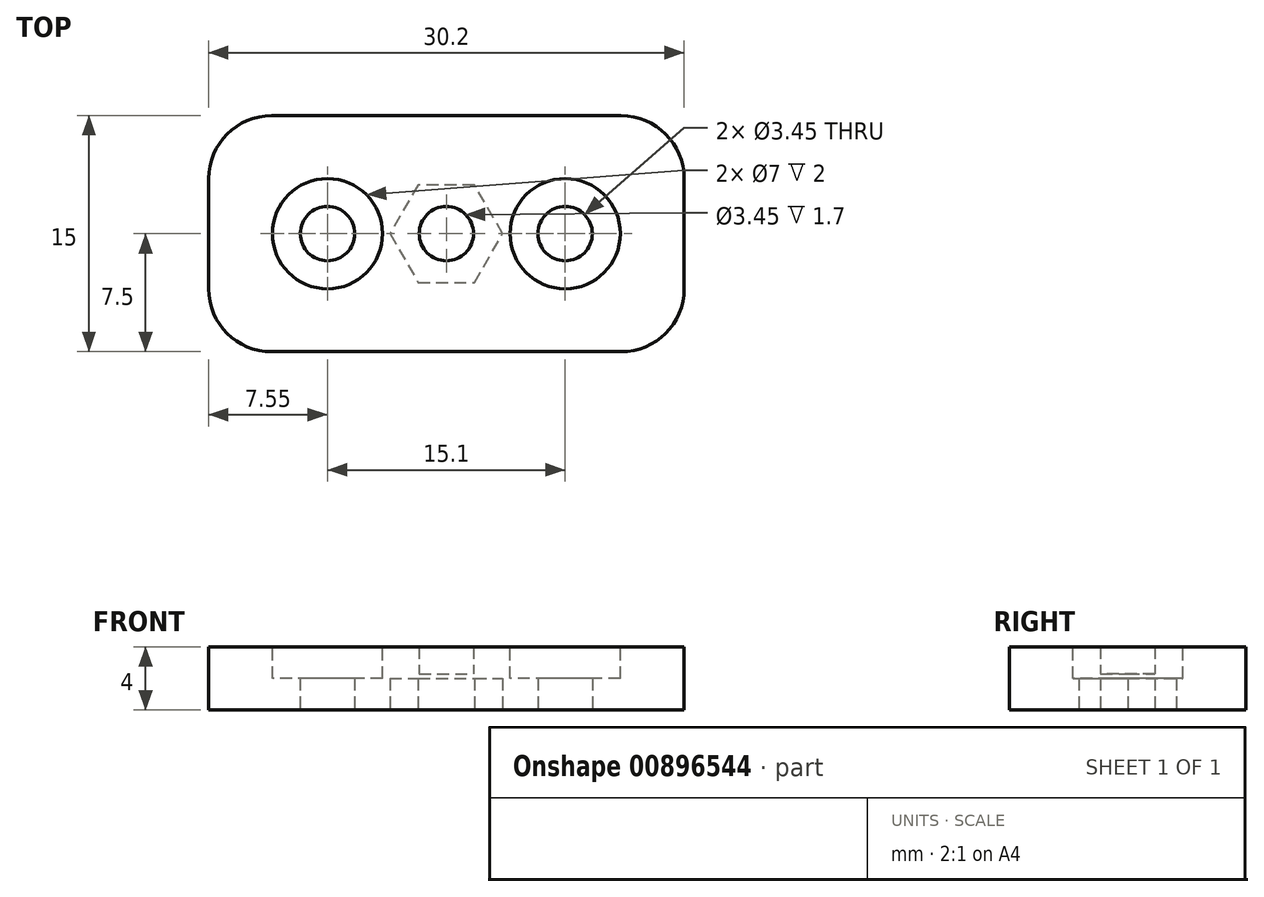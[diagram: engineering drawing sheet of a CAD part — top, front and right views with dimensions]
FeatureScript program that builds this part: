
annotation { "Feature Type Name" : "Feature", "Feature Type Description" : "" }
export const myFeature = defineFeature(function(context is Context, id is Id, definition is map)
    precondition{}
    {
        {
            var Q0;
            Q0=qCreatedBy(makeId("Top.planeOp"),FACE);
            var sketch = newSketch(context, id + "F0", { "sketchPlane" : qUnion([Q0])});
            skLineSegment(sketch, "E0.bottom", {"start": v(0, 0) * mm, "end": v(30.2, 0) * mm});
            skLineSegment(sketch, "E0.top", {"start": v(0, 15) * mm, "end": v(30.2, 15) * mm});
            skLineSegment(sketch, "E0.left", {"start": v(0, 0) * mm, "end": v(0, 15) * mm});
            skLineSegment(sketch, "E0.right", {"start": v(30.2, 0) * mm, "end": v(30.2, 15) * mm});
            skLineSegment(sketch, "E1", {"start": v(15.1, 0) * mm, "end": v(15.1, 15) * mm, "construction": true});
            skCircle(sketch, "E2", {"center": v(7.55, 7.5) * mm, "radius": 1.73 * mm});
            skCircle(sketch, "E3", {"center": v(22.65, 7.5) * mm, "radius": 1.73 * mm});
            skLineSegment(sketch, "E4", {"start": v(7.55, 7.5) * mm, "end": v(15.1, 7.5) * mm, "construction": true});
            skLineSegment(sketch, "E5", {"start": v(15.1, 7.5) * mm, "end": v(22.65, 7.5) * mm, "construction": true});
            skCircle(sketch, "E6", {"center": v(15.1, 7.5) * mm, "radius": 1.73 * mm});
            skSolve(sketch);
        }
        {
            var Q0;
            Q0 = qSketchRegion(id + "F0", true);
            extrude(context, id + "F1", {"entities" : qUnion([Q0]), "depth" : 4 * mm, "offsetDistance" : 25 * mm});
        }
        {
            var Q0;
            Q0=makeQuery(id+"F1.opExtrude","CAP_FACE",FACE,{"disambiguationData":[OSD([sQuery(id+"F0.wireOp",EDGE,"E0.bottom"),sQuery(id+"F0.wireOp",EDGE,"E0.top"),sQuery(id+"F0.wireOp",EDGE,"E0.left"),sQuery(id+"F0.wireOp",EDGE,"E0.right"),sQuery(id+"F0.wireOp",EDGE,"E2"),sQuery(id+"F0.wireOp",EDGE,"E3"),sQuery(id+"F0.wireOp",EDGE,"E6")])],"isStart":false});
            var sketch = newSketch(context, id + "F2", { "sketchPlane" : qUnion([Q0])});
            skCircle(sketch, "E7", {"center": v(7.55, 7.5) * mm, "radius": 3.5 * mm});
            skCircle(sketch, "E8", {"center": v(22.65, 7.5) * mm, "radius": 3.5 * mm});
            skSolve(sketch);
        }
        {
            var Q0;
            Q0 = qSketchRegion(id + "F2", true);
            extrude(context, id + "F3", {"entities" : qUnion([Q0]), "operationType" : NewBodyOperationType.REMOVE, "oppositeDirection" : true, "depth" : 2 * mm, "offsetDistance" : 25 * mm});
        }
        {
            var Q0;
            Q0=makeQuery(id+"F1.opExtrude","CAP_FACE",FACE,{"disambiguationData":[OSD([sQuery(id+"F0.wireOp",EDGE,"E0.bottom"),sQuery(id+"F0.wireOp",EDGE,"E0.top"),sQuery(id+"F0.wireOp",EDGE,"E0.left"),sQuery(id+"F0.wireOp",EDGE,"E0.right"),sQuery(id+"F0.wireOp",EDGE,"E2"),sQuery(id+"F0.wireOp",EDGE,"E3"),sQuery(id+"F0.wireOp",EDGE,"E6")])],"isStart":true});
            var sketch = newSketch(context, id + "F4", { "sketchPlane" : qUnion([Q0])});
            skCircle(sketch, "E9.cCircle", {"center": v(15.1, -7.5) * mm, "radius": 3.1 * mm, "construction": true});
            skLineSegment(sketch, "E9.0", {"start": v(16.89, -4.4) * mm, "end": v(18.68, -7.5) * mm});
            skLineSegment(sketch, "E9.1", {"start": v(18.68, -7.5) * mm, "end": v(16.89, -10.6) * mm});
            skLineSegment(sketch, "E9.2", {"start": v(16.89, -10.6) * mm, "end": v(13.31, -10.6) * mm});
            skLineSegment(sketch, "E9.3", {"start": v(13.31, -10.6) * mm, "end": v(11.52, -7.5) * mm});
            skLineSegment(sketch, "E9.4", {"start": v(11.52, -7.5) * mm, "end": v(13.31, -4.4) * mm});
            skLineSegment(sketch, "E9.5", {"start": v(13.31, -4.4) * mm, "end": v(16.89, -4.4) * mm});
            skPoint(sketch, "E9.0.midPoint", {"position": v(17.78, -5.95) * mm});
            skSolve(sketch);
        }
        {
            var Q0;
            Q0 = qSketchRegion(id + "F4", true);
            extrude(context, id + "F5", {"entities" : qUnion([Q0]), "operationType" : NewBodyOperationType.REMOVE, "oppositeDirection" : true, "depth" : 2 * mm, "offsetDistance" : 25 * mm});
        }
        {
            var Q0;
            Q0=makeQuery(id+"F5.boolean.opBoolean","COPY",FACE,{"derivedFrom":makeQuery(id+"F5.opExtrude","CAP_FACE",FACE,{"disambiguationData":[OSD([sQuery(id+"F4.wireOp",EDGE,"E9.0"),sQuery(id+"F4.wireOp",EDGE,"E9.1"),sQuery(id+"F4.wireOp",EDGE,"E9.2"),sQuery(id+"F4.wireOp",EDGE,"E9.3"),sQuery(id+"F4.wireOp",EDGE,"E9.4"),sQuery(id+"F4.wireOp",EDGE,"E9.5")])],"isStart":false})});
            var sketch = newSketch(context, id + "F6", { "sketchPlane" : qUnion([Q0])});
            skCircle(sketch, "E10", {"center": v(15.1, -7.5) * mm, "radius": 1.75 * mm});
            skSolve(sketch);
        }
        {
            var Q0;
            Q0 = qSketchRegion(id + "F6", true);
            extrude(context, id + "F7", {"entities" : qUnion([Q0]), "operationType" : NewBodyOperationType.ADD, "oppositeDirection" : true, "depth" : 0.3 * mm, "offsetDistance" : 25 * mm});
        }
        {
            var Q0;
            Q0=makeQuery(id+"F1.opExtrude","SWEPT_EDGE",EDGE,{"disambiguationData":[OSD([sQuery(id+"F0.wireOp",EDGE,"E0.bottom"),sQuery(id+"F0.wireOp",EDGE,"E0.left")])]});
            var Q1;
            Q1=makeQuery(id+"F1.opExtrude","SWEPT_EDGE",EDGE,{"disambiguationData":[OSD([sQuery(id+"F0.wireOp",EDGE,"E0.bottom"),sQuery(id+"F0.wireOp",EDGE,"E0.right")])]});
            var Q2;
            Q2=makeQuery(id+"F1.opExtrude","SWEPT_EDGE",EDGE,{"disambiguationData":[OSD([sQuery(id+"F0.wireOp",EDGE,"E0.top"),sQuery(id+"F0.wireOp",EDGE,"E0.right")])]});
            var Q3;
            Q3=makeQuery(id+"F1.opExtrude","SWEPT_EDGE",EDGE,{"disambiguationData":[OSD([sQuery(id+"F0.wireOp",EDGE,"E0.top"),sQuery(id+"F0.wireOp",EDGE,"E0.left")])]});
            fillet(context, id + "F8", {"entities" : qUnion([Q0, Q1, Q2, Q3]), "radius" : 4 * mm, "tangentPropagation" : true, "allowEdgeOverflow" : false});
        }
    });
